# Revit family: Bottle_Filler-Murdock-H2O-To-Go-BFI1-BF12_Series
name_source: partatom
category: Plumbing Fixtures
revit_build: Autodesk Revit 2018 (Build: 20170223_1515(x64)
units: mm (PartAtom-declared; Revit-internal decimal feet)

## family parameters
Cut with Voids When Loaded = Yes
Host = Face
OmniClass Number = 23.65.70.14.11
OmniClass Title = Drinking Fountains/Coolers
Part Type = Normal
Room Calculation Point = No
Round Connector Dimension = Use Diameter
Shared = Yes

## types (4) — shared parameters
-WF1 1500-gallon capacity, NSF 42+53,1 micron Lead Reduction Filter = No
ADA Compliant = Yes
Assembly Code = D2010820
CW Connection = Yes
CWFU = 1.5
Cold Water Connection Diameter = 3/8"
Cold Water Connection Height = 19 3/8"
Cold Water Connection Radius = 3/16"
Cold Water Connection Width = 2"
Default Elevation = 0"
Flow Rate = 1.00 GPM
HW Connection = No
HWFU = 1.5
Height = 19 1/8"
Housing Material = Stainless Steel-Murdock-Satin
IAPMO Compliance = Optional -WF1 has NSF/ANSI 42 & 53 certification
Inner Panel Material = Steel-Murdock-Galvannealed
Installation Type = Wall Mounted
Length = 18 1/4"
Manufacturer = Murdock Mfg.
Material = Stainless Steel-Murdock-Satin
Mounting Height From Floor LVL = 30 5/8"
Price = Prices may vary. Please consult Manufacturer Representative for most up-to-date price list.
Product Documentation Link = https://www.murdockmfg.com
Product Page URL = https://www.murdockmfg.com
URL = https://www.murdockmfg.com
Vent Connection = No
WFU = 2
Warranty Information = Murdock Mfg.™ warrants that its products are free from defects in material or workmanship under normal use and service for a period of 18 months from date of shipment.
Waste Connection = No
Width = 3 1/8"

## per-type parameters (varying)
| type | BAT Battery Powered Operation | BCD - Bottle Counter Display | Description | Maximum Run Time | Pushbutton Visibility | Sensor Visibility | Transformer Specification | Type Comments |
| BF11 | No | No | Push Button Deck Mount H2O to Go!® Bottler Filler |  | Yes | No |  | This push button activated bottle filler connects to a A17 Water Cooler. |
| BF12 | No | No | H2O-To-Go!® Sensor-Operated Water Refill Station (A17/A19 Add-On) | 20 Seconds | No | Yes | 120VAC/9V DC Plug-In Transformer | This sensor activted bottle filler connects to a A17 Water Cooler. |
| BF12-BAT | Yes | No | H2O-To-Go!® Sensor-Operated Water Refill Station (A17/A19 Add-On) | 20 Seconds | No | Yes | 120VAC/9V DC Plug-In Transformer | This sensor activted bottle filler connects to a A17 Water Cooler. |
| BF12-BCD | No | Yes | H2O-To-Go!® Sensor-Operated Water Refill Station (A17/A19 Add-On) | 20 Seconds | No | Yes | 120VAC/9V DC Plug-In Transformer | This sensor activted bottle filler connects to a A17 Water Cooler. |

note: column(s) folded — value = type name in every type: Model

## geometry (parser evidence)
native form markers: Sweep x3
no freeform markers — native parametric forms only
